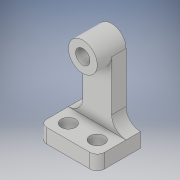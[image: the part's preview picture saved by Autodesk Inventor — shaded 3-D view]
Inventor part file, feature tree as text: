
AUTODESK INVENTOR PART (.ipt)
format: ipt  version: 2018 (Build 220112000, 112)  size: 186,368 bytes
history: native  units: in
note: dims shown in document units (in); Inventor stores cm internally (conversion verified against a paired STEP export)
features: sketch x7, extrude x6, projected_geometry x6, fillet x2, hole x1
ambient origin geometry x8: Origin, YZ Plane, XZ Plane, XY Plane, X Axis, Y Axis, Z Axis, Center Point
bodies: Solid1 (feature_tree)
feature tree (22):
  extrude  "Extrusion1"  Depth=2.0in
  extrude  "Extrusion2"  Depth=1.0in
  extrude  "Extrusion3"  Depth=1.5in TaperAngle=0.0deg
  extrude  "Extrusion4"  Depth=0.5in
  extrude  "Extrusion5"  Depth=0.5in
  extrude  "Extrusion6"  Depth=0.5in
  hole  "Hole1"  [1 undecoded]
  fillet  "Fillet1"  Radius=1.0in
  fillet  "Fillet2"  Radius=0.25in
  sketch  "Sketch1"  dims[d0=2.0in d1=3.25in]
  sketch  "Sketch2"  dims[d2=1.5in d3=0.0in d4=1.0in]
  sketch  "Sketch3"  dims[d5=2.75in d6=1.5in d7=0.0in]
  sketch  "Sketch4"  dims[d8=0.5in d9=2.75in]
  projected_geometry  "Projected Loop1"
  sketch  "Sketch5"  dims[d10=0.5in d11=2.75in]
  projected_geometry  "Projected Loop2"
  projected_geometry  "Projected Loop3"
  sketch  "Sketch6"  dims[d12=1.5in d13=0.0in d14=0.5in]
  projected_geometry  "Projected Loop4"
  sketch  "Sketch7"  dims[d15=1.0in d16=0.0in d17=1.0in d18=0.0in d19=1.0in d20=0.0in d21=0.5in d22=0.75in d23=0.375in d24=0.25in d25=0.5635in d26=1.0in d27=0.8108in d28=0.25in d29=0.5in]
  projected_geometry  "Projected Loop5"
  projected_geometry  "Projected Loop6"
note: 1 required parameter value undecoded (feature->parameter linkage not recoverable at this tier; creation-order binding heuristic only, values carry confidence <= 0.55)
